# Revit family: Peak 380 Armarmatur
name_source: partatom
category: Lighting Fixtures
revit_build: Autodesk Revit 2015 (Build: 20140903_1530(x64)
units: mm (PartAtom-declared; Revit-internal decimal feet)

## types (72) — shared parameters
BIMobject category = Outside
Classification = IP 66, class II
Color Filter = 16777215
Colour accuracy = 4 steps SDCM
Colour rendering = min 70 Ra, typically 75 Ra
Connection = In the pole.The luminaire is delivered with lead according to pole height, 2x1.5 mm2
Corrosion class = C5
Design country = Denmark
Dimming = 8-100% in time intervals or 1-10 V, DALI, Line switch, AmpDim
Dimming Lamp Color Temperature Shift = <None>
Edition number = 1
Emit Shape Visible in Rendering = No
Emit from Circle Diameter = 300 mm
Height = 114 mm  [stored 0.374016 ft]
IFC Classification = Light Fixture
Impact resistance = IK08
Installation instructions = http://www.focus-lighting.dk
Length = 490 mm  [stored 1.60761 ft]
Manufacturer = Focus Lighting
Manufacturer country = Denmark
Manufacturer name = Focus Lighting
Material Secondary = Glass-Nyx
Mounting = On conical pole, 60 or 76 mm top diameter,
Nominal height = 114
Nominal width = 380
Operational life = min. 80,000 hours at ta max 25°, L80B10
Operationel life = min 100,000 hours
Product Data Url = https://bimobject.com
Product Guid = e5eea86c-a8f0-42d5-a2a8-c1225b159391
Product SKU = peak380
Product family = Outdoor
Product group = Columns
QR code = http://bimobject.com
Shade = 3 mm hardened glass, coated on the edge
Surge protection = L/N-GND: 8 kV, L-N: 6 kV
Technical description = http://www.focus-lighting.dk
Temperature range = -30 to +35° C
Tilt Angle = 90.00°
UNSPSC Code = 3911
URL = http://bimobject.com
Voltage = 220
Wattage Comments = max 85 W
Weight = 6-7 kg
Weight Net (Kg) = 7
Width = 380 mm  [stored 1.24672 ft]
zero-valued in all types: Cost

## per-type parameters (varying)
| type | Driver | Inrush current | LED with lenses | Lamp | Material Main | Output ratio | Photometric Web File |
| 8890-4740U | Xitanium Full Xi FP 40 W 0.2-0.7 A, programmable | max 22 A (50% after 290 µs) | FastFlex (FF) type III, 1, 2, or 3 modules | 1xFF type III | FocusLighting_GraphiteGrey | 91% | Peak_2xFFg3_III-X_730_LDT.ies |
| 8890-4730U | Xitanium Full Xi FP 40 W 0.2-0.7 A, programmable | max 22 A (50% after 290 µs) | FastFlex (FF) type III, 1, 2, or 3 modules | 1xFF type III | FocusLighting_GraphiteGrey | 91% | Peak_2xFFg3_III-X_730_LDT.ies |
| 8889-3730U | Xitanium Full Xi FP 150 W 0.2-0.7 A, programmable | max 53 A (50% after 300 µs) | FastFlex (FF) type PX, 1, 2, or 3 modules | 3xFF type PX | FocusLighting_Black | 90-94% | Peak_2xFFg3DA_PX_730_LDT.ies |
| 8889-3740U | Xitanium Full Xi FP 150 W 0.2-0.7 A, programmable | max 53 A (50% after 300 µs) | FastFlex (FF) type PX, 1, 2, or 3 modules | 3xFF type PX | FocusLighting_Black | 90-94% | Peak_2xFFg3DA_PX_730_LDT.ies |
| 8889-4730U | Xitanium Full Xi FP 150 W 0.2-0.7 A, programmable | max 53 A (50% after 300 µs) | FastFlex (FF) type PX, 1, 2, or 3 modules | 3xFF type PX | FocusLighting_GraphiteGrey | 90-94% | Peak_2xFFg3DA_PX_730_LDT.ies |
| 8889-4740U | Xitanium Full Xi FP 150 W 0.2-0.7 A, programmable | max 53 A (50% after 300 µs) | FastFlex (FF) type PX, 1, 2, or 3 modules | 3xFF type PX | FocusLighting_GraphiteGrey | 90-94% | Peak_2xFFg3DA_PX_730_LDT.ies |
| 8889-9730U | Xitanium Full Xi FP 150 W 0.2-0.7 A, programmable | max 53 A (50% after 300 µs) | FastFlex (FF) type PX, 1, 2, or 3 modules | 3xFF type PX | FocusLighting_SilverGrey | 90-94% | Peak_2xFFg3DA_PX_730_LDT.ies |
| 8889-9740U | Xitanium Full Xi FP 150 W 0.2-0.7 A, programmable | max 53 A (50% after 300 µs) | FastFlex (FF) type PX, 1, 2, or 3 modules | 3xFF type PX | FocusLighting_SilverGrey | 90-94% | Peak_2xFFg3DA_PX_730_LDT.ies |
| 8888-3730U | Xitanium Full Xi FP 75 W 0.2-0.7 A, programmable | max 46 A (50% after 250 µs) | FastFlex (FF) type PX, 1, 2, or 3 modules | 2xFF type PX | FocusLighting_Black | 90-94% | Peak_2xFFg3DA_PX_730_LDT.ies |
| 8888-3740U | Xitanium Full Xi FP 75 W 0.2-0.7 A, programmable | max 46 A (50% after 250 µs) | FastFlex (FF) type PX, 1, 2, or 3 modules | 2xFF type PX | FocusLighting_Black | 90-94% | Peak_2xFFg3DA_PX_730_LDT.ies |
| 8888-4730U | Xitanium Full Xi FP 75 W 0.2-0.7 A, programmable | max 46 A (50% after 250 µs) | FastFlex (FF) type PX, 1, 2, or 3 modules | 2xFF type PX | FocusLighting_GraphiteGrey | 90-94% | Peak_2xFFg3DA_PX_730_LDT.ies |
| 8888-4740U | Xitanium Full Xi FP 75 W 0.2-0.7 A, programmable | max 46 A (50% after 250 µs) | FastFlex (FF) type PX, 1, 2, or 3 modules | 2xFF type PX | FocusLighting_GraphiteGrey | 90-94% | Peak_2xFFg3DA_PX_730_LDT.ies |
| 8888-9730U | Xitanium Full Xi FP 75 W 0.2-0.7 A, programmable | max 46 A (50% after 250 µs) | FastFlex (FF) type PX, 1, 2, or 3 modules | 2xFF type PX | FocusLighting_SilverGrey | 90-94% | Peak_2xFFg3DA_PX_730_LDT.ies |
| 8888-9740U | Xitanium Full Xi FP 75 W 0.2-0.7 A, programmable | max 46 A (50% after 250 µs) | FastFlex (FF) type PX, 1, 2, or 3 modules | 2xFF type PX | FocusLighting_SilverGrey | 90-94% | Peak_2xFFg3DA_PX_730_LDT.ies |
| 8887-3730U | Xitanium Full Xi FP 40 W 0.2-0.7 A, programmable | max 22 A (50% after 290 µs) | FastFlex (FF) type PX, 1, 2, or 3 modules | 1xFF type PX | FocusLighting_Black | 90-94% | Peak_2xFFg3DA_PX_730_LDT.ies |
| 8887-3740U | Xitanium Full Xi FP 40 W 0.2-0.7 A, programmable | max 22 A (50% after 290 µs) | FastFlex (FF) type PX, 1, 2, or 3 modules | 1xFF type PX | FocusLighting_Black | 90-94% | Peak_2xFFg3DA_PX_730_LDT.ies |
| 8887-4730U | Xitanium Full Xi FP 40 W 0.2-0.7 A, programmable | max 22 A (50% after 290 µs) | FastFlex (FF) type PX, 1, 2, or 3 modules | 1xFF type PX | FocusLighting_GraphiteGrey | 90-94% | Peak_2xFFg3DA_PX_730_LDT.ies |
| 8887-4740U | Xitanium Full Xi FP 40 W 0.2-0.7 A, programmable | max 22 A (50% after 290 µs) | FastFlex (FF) type PX, 1, 2, or 3 modules | 1xFF type PX | FocusLighting_GraphiteGrey | 90-94% | Peak_2xFFg3DA_PX_730_LDT.ies |
| 8887-9730U | Xitanium Full Xi FP 40 W 0.2-0.7 A, programmable | max 22 A (50% after 290 µs) | FastFlex (FF) type PX, 1, 2, or 3 modules | 1xFF type PX | FocusLighting_SilverGrey | 90-94% | Peak_2xFFg3DA_PX_730_LDT.ies |
| 8887-9740U | Xitanium Full Xi FP 40 W 0.2-0.7 A, programmable | max 22 A (50% after 290 µs) | FastFlex (FF) type PX, 1, 2, or 3 modules | 1xFF type PX | FocusLighting_SilverGrey | 90-94% | Peak_2xFFg3DA_PX_730_LDT.ies |
| 8898-3730U | Xitanium Full Xi FP 150 W 0.2-0.7 A, programmable | max 53 A (50% after 300 µs) | FastFlex (FF) type IV, 1, 2, or 3 modules | 3xFF type IV | FocusLighting_Black | 90-94% | Peak_2xFFg3_IV-X_730_LDT.ies |
| 8898-3740U | Xitanium Full Xi FP 150 W 0.2-0.7 A, programmable | max 53 A (50% after 300 µs) | FastFlex (FF) type IV, 1, 2, or 3 modules | 3xFF type IV | FocusLighting_Black | 90-94% | Peak_2xFFg3_IV-X_730_LDT.ies |
| 8898-4730U | Xitanium Full Xi FP 150 W 0.2-0.7 A, programmable | max 53 A (50% after 300 µs) | FastFlex (FF) type IV, 1, 2, or 3 modules | 3xFF type IV | FocusLighting_GraphiteGrey | 90-94% | Peak_2xFFg3_IV-X_730_LDT.ies |
| 8898-4740U | Xitanium Full Xi FP 150 W 0.2-0.7 A, programmable | max 53 A (50% after 300 µs) | FastFlex (FF) type IV, 1, 2, or 3 modules | 3xFF type IV | FocusLighting_GraphiteGrey | 90-94% | Peak_2xFFg3_IV-X_730_LDT.ies |
| 8898-9730U | Xitanium Full Xi FP 150 W 0.2-0.7 A, programmable | max 53 A (50% after 300 µs) | FastFlex (FF) type IV, 1, 2, or 3 modules | 3xFF type IV | FocusLighting_SilverGrey | 90-94% | Peak_2xFFg3_IV-X_730_LDT.ies |
| 8898-9740U | Xitanium Full Xi FP 150 W 0.2-0.7 A, programmable | max 53 A (50% after 300 µs) | FastFlex (FF) type IV, 1, 2, or 3 modules | 3xFF type IV | FocusLighting_SilverGrey | 90-94% | Peak_2xFFg3_IV-X_730_LDT.ies |
| 8897-3730U | Xitanium Full Xi FP 75 W 0.2-0.7 A, programmable | max 46 A (50% after 250 µs) | FastFlex (FF) type IV, 1, 2, or 3 modules | 2xFF type IV | FocusLighting_Black | 90-94% | Peak_2xFFg3_IV-X_730_LDT.ies |
| 8897-3740U | Xitanium Full Xi FP 75 W 0.2-0.7 A, programmable | max 46 A (50% after 250 µs) | FastFlex (FF) type IV, 1, 2, or 3 modules | 2xFF type IV | FocusLighting_Black | 90-94% | Peak_2xFFg3_IV-X_730_LDT.ies |
| 8897-4730U | Xitanium Full Xi FP 75 W 0.2-0.7 A, programmable | max 46 A (50% after 250 µs) | FastFlex (FF) type IV, 1, 2, or 3 modules | 2xFF type IV | FocusLighting_GraphiteGrey | 90-94% | Peak_2xFFg3_IV-X_730_LDT.ies |
| 8897-4740U | Xitanium Full Xi FP 75 W 0.2-0.7 A, programmable | max 46 A (50% after 250 µs) | FastFlex (FF) type IV, 1, 2, or 3 modules | 2xFF type IV | FocusLighting_GraphiteGrey | 90-94% | Peak_2xFFg3_IV-X_730_LDT.ies |
| 8897-9730U | Xitanium Full Xi FP 75 W 0.2-0.7 A, programmable | max 46 A (50% after 250 µs) | FastFlex (FF) type IV, 1, 2, or 3 modules | 2xFF type IV | FocusLighting_SilverGrey | 90-94% | Peak_2xFFg3_IV-X_730_LDT.ies |
| 8897-9740U | Xitanium Full Xi FP 75 W 0.2-0.7 A, programmable | max 46 A (50% after 250 µs) | FastFlex (FF) type IV, 1, 2, or 3 modules | 2xFF type IV | FocusLighting_SilverGrey | 90-94% | Peak_2xFFg3_IV-X_730_LDT.ies |
| 8896-3730U | Xitanium Full Xi FP 40 W 0.2-0.7 A, programmable | max 22 A (50% after 290 µs) | FastFlex (FF) type IV, 1, 2, or 3 modules | 1xFF type IV | FocusLighting_Black | 90-94% | Peak_2xFFg3_IV-X_730_LDT.ies |
| 8896-3740U | Xitanium Full Xi FP 40 W 0.2-0.7 A, programmable | max 22 A (50% after 290 µs) | FastFlex (FF) type IV, 1, 2, or 3 modules | 1xFF type IV | FocusLighting_Black | 90-94% | Peak_2xFFg3_IV-X_730_LDT.ies |
| 8896-4730U | Xitanium Full Xi FP 40 W 0.2-0.7 A, programmable | max 22 A (50% after 290 µs) | FastFlex (FF) type IV, 1, 2, or 3 modules | 1xFF type IV | FocusLighting_GraphiteGrey | 90-94% | Peak_2xFFg3_IV-X_730_LDT.ies |
| 8896-4740U | Xitanium Full Xi FP 40 W 0.2-0.7 A, programmable | max 22 A (50% after 290 µs) | FastFlex (FF) type IV, 1, 2, or 3 modules | 1xFF type IV | FocusLighting_GraphiteGrey | 90-94% | Peak_2xFFg3_IV-X_730_LDT.ies |
| 8896-9730U | Xitanium Full Xi FP 40 W 0.2-0.7 A, programmable | max 22 A (50% after 290 µs) | FastFlex (FF) type IV, 1, 2, or 3 modules | 1xFF type IV | FocusLighting_SilverGrey | 90-94% | Peak_2xFFg3_IV-X_730_LDT.ies |
| 8896-9740U | Xitanium Full Xi FP 40 W 0.2-0.7 A, programmable | max 22 A (50% after 290 µs) | FastFlex (FF) type IV, 1, 2, or 3 modules | 1xFF type IV | FocusLighting_SilverGrey | 90-94% | Peak_2xFFg3_IV-X_730_LDT.ies |
| 8895-3730U | Xitanium Full Xi FP 150 W 0.2-0.7 A, programmable | max 53 A (50% after 300 µs) | FastFlex (FF) type II-XWTR, 1, 2, or 3 modules | 3xFF type II-XWTR | FocusLighting_Black | 94% | Peak_2xFFg3_II-X WTR_730_LDT.ies |
| 8895-3740U | Xitanium Full Xi FP 150 W 0.2-0.7 A, programmable | max 53 A (50% after 300 µs) | FastFlex (FF) type II-XWTR, 1, 2, or 3 modules | 3xFF type II-XWTR | FocusLighting_Black | 94% | Peak_2xFFg3_II-X WTR_730_LDT.ies |
| 8895-4730U | Xitanium Full Xi FP 150 W 0.2-0.7 A, programmable | max 53 A (50% after 300 µs) | FastFlex (FF) type II-XWTR, 1, 2, or 3 modules | 3xFF type II-XWTR | FocusLighting_GraphiteGrey | 94% | Peak_2xFFg3_II-X WTR_730_LDT.ies |
| 8895-4740U | Xitanium Full Xi FP 150 W 0.2-0.7 A, programmable | max 53 A (50% after 300 µs) | FastFlex (FF) type II-XWTR, 1, 2, or 3 modules | 3xFF type II-XWTR | FocusLighting_GraphiteGrey | 94% | Peak_2xFFg3_II-X WTR_730_LDT.ies |
| 8895-9730U | Xitanium Full Xi FP 150 W 0.2-0.7 A, programmable | max 53 A (50% after 300 µs) | FastFlex (FF) type II-XWTR, 1, 2, or 3 modules | 3xFF type II-XWTR | FocusLighting_SilverGrey | 94% | Peak_2xFFg3_II-X WTR_730_LDT.ies |
| 8895-9740U | Xitanium Full Xi FP 150 W 0.2-0.7 A, programmable | max 53 A (50% after 300 µs) | FastFlex (FF) type II-XWTR, 1, 2, or 3 modules | 3xFF type II-XWTR | FocusLighting_SilverGrey | 94% | Peak_2xFFg3_II-X WTR_730_LDT.ies |
| 8894-3730U | Xitanium Full Xi FP 75 W 0.2-0.7 A, programmable | max 46 A (50% after 250 µs) | FastFlex (FF) type II-XWTR, 1, 2, or 3 modules | 2xFF type II-XWTR | FocusLighting_Black | 94% | Peak_2xFFg3_II-X WTR_730_LDT.ies |
| 8894-3740U | Xitanium Full Xi FP 75 W 0.2-0.7 A, programmable | max 46 A (50% after 250 µs) | FastFlex (FF) type II-XWTR, 1, 2, or 3 modules | 2xFF type II-XWTR | FocusLighting_Black | 94% | Peak_2xFFg3_II-X WTR_730_LDT.ies |
| 8894-4730U | Xitanium Full Xi FP 75 W 0.2-0.7 A, programmable | max 46 A (50% after 250 µs) | FastFlex (FF) type II-XWTR, 1, 2, or 3 modules | 2xFF type II-XWTR | FocusLighting_GraphiteGrey | 94% | Peak_2xFFg3_II-X WTR_730_LDT.ies |
| 8894-4740U | Xitanium Full Xi FP 75 W 0.2-0.7 A, programmable | max 46 A (50% after 250 µs) | FastFlex (FF) type II-XWTR, 1, 2, or 3 modules | 2xFF type II-XWTR | FocusLighting_GraphiteGrey | 94% | Peak_2xFFg3_II-X WTR_730_LDT.ies |
| 8894-9730U | Xitanium Full Xi FP 75 W 0.2-0.7 A, programmable | max 46 A (50% after 250 µs) | FastFlex (FF) type II-XWTR, 1, 2, or 3 modules | 2xFF type II-XWTR | FocusLighting_SilverGrey | 94% | Peak_2xFFg3_II-X WTR_730_LDT.ies |
| 8894-9740U | Xitanium Full Xi FP 75 W 0.2-0.7 A, programmable | max 46 A (50% after 250 µs) | FastFlex (FF) type II-XWTR, 1, 2, or 3 modules | 2xFF type II-XWTR | FocusLighting_SilverGrey | 94% | Peak_2xFFg3_II-X WTR_730_LDT.ies |
| 8893-3730U | Xitanium Full Xi FP 40 W 0.2-0.7 A, programmable | max 22 A (50% after 290 µs) | FastFlex (FF) type II-XWTR, 1, 2, or 3 modules | 1xFF type II-XWTR | FocusLighting_Black | 94% | Peak_2xFFg3_II-X WTR_730_LDT.ies |
| 8893-3740U | Xitanium Full Xi FP 40 W 0.2-0.7 A, programmable | max 22 A (50% after 290 µs) | FastFlex (FF) type II-XWTR, 1, 2, or 3 modules | 1xFF type II-XWTR | FocusLighting_Black | 94% | Peak_2xFFg3_II-X WTR_730_LDT.ies |
| 8893-4730U | Xitanium Full Xi FP 40 W 0.2-0.7 A, programmable | max 22 A (50% after 290 µs) | FastFlex (FF) type II-XWTR, 1, 2, or 3 modules | 1xFF type II-XWTR | FocusLighting_GraphiteGrey | 94% | Peak_2xFFg3_II-X WTR_730_LDT.ies |
| 8893-4740U | Xitanium Full Xi FP 40 W 0.2-0.7 A, programmable | max 22 A (50% after 290 µs) | FastFlex (FF) type II-XWTR, 1, 2, or 3 modules | 1xFF type II-XWTR | FocusLighting_GraphiteGrey | 94% | Peak_2xFFg3_II-X WTR_730_LDT.ies |
| 8893-9730U | Xitanium Full Xi FP 40 W 0.2-0.7 A, programmable | max 22 A (50% after 290 µs) | FastFlex (FF) type II-XWTR, 1, 2, or 3 modules | 1xFF type II-XWTR | FocusLighting_SilverGrey | 94% | Peak_2xFFg3_II-X WTR_730_LDT.ies |
| 8893-9740U | Xitanium Full Xi FP 40 W 0.2-0.7 A, programmable | max 22 A (50% after 290 µs) | FastFlex (FF) type II-XWTR, 1, 2, or 3 modules | 1xFF type II-XWTR | FocusLighting_SilverGrey | 94% | Peak_2xFFg3_II-X WTR_730_LDT.ies |
| 8892-3730U | Xitanium Full Xi FP 150 W 0.2-0.7 A, programmable | max 53 A (50% after 300 µs) | FastFlex (FF) type III, 1, 2, or 3 modules | 3xFF type III | FocusLighting_Black | 91% | Peak_2xFFg3_III-X_730_LDT.ies |
| 8892-3740U | Xitanium Full Xi FP 150 W 0.2-0.7 A, programmable | max 53 A (50% after 300 µs) | FastFlex (FF) type III, 1, 2, or 3 modules | 3xFF type III | FocusLighting_Black | 91% | Peak_2xFFg3_III-X_730_LDT.ies |
| 8892-4730U | Xitanium Full Xi FP 150 W 0.2-0.7 A, programmable | max 53 A (50% after 300 µs) | FastFlex (FF) type III, 1, 2, or 3 modules | 3xFF type III | FocusLighting_GraphiteGrey | 91% | Peak_2xFFg3_III-X_730_LDT.ies |
| 8892-4740U | Xitanium Full Xi FP 150 W 0.2-0.7 A, programmable | max 53 A (50% after 300 µs) | FastFlex (FF) type III, 1, 2, or 3 modules | 3xFF type III | FocusLighting_GraphiteGrey | 91% | Peak_2xFFg3_III-X_730_LDT.ies |
| 8892-9730U | Xitanium Full Xi FP 150 W 0.2-0.7 A, programmable | max 53 A (50% after 300 µs) | FastFlex (FF) type III, 1, 2, or 3 modules | 3xFF type III | FocusLighting_SilverGrey | 91% | Peak_2xFFg3_III-X_730_LDT.ies |
| 8892-9740U | Xitanium Full Xi FP 150 W 0.2-0.7 A, programmable | max 53 A (50% after 300 µs) | FastFlex (FF) type III, 1, 2, or 3 modules | 3xFF type III | FocusLighting_SilverGrey | 91% | Peak_2xFFg3_III-X_730_LDT.ies |
| 8891-3730U | Xitanium Full Xi FP 75 W 0.2-0.7 A, programmable | max 46 A (50% after 250 µs) | FastFlex (FF) type III, 1, 2, or 3 modules | 2xFF type III | FocusLighting_Black | 91% | Peak_2xFFg3_III-X_730_LDT.ies |
| 8891-3740U | Xitanium Full Xi FP 75 W 0.2-0.7 A, programmable | max 46 A (50% after 250 µs) | FastFlex (FF) type III, 1, 2, or 3 modules | 2xFF type III | FocusLighting_Black | 91% | Peak_2xFFg3_III-X_730_LDT.ies |
| 8891-4730U | Xitanium Full Xi FP 75 W 0.2-0.7 A, programmable | max 46 A (50% after 250 µs) | FastFlex (FF) type III, 1, 2, or 3 modules | 2xFF type III | FocusLighting_GraphiteGrey | 91% | Peak_2xFFg3_III-X_730_LDT.ies |
| 8891-4740U | Xitanium Full Xi FP 75 W 0.2-0.7 A, programmable | max 46 A (50% after 250 µs) | FastFlex (FF) type III, 1, 2, or 3 modules | 2xFF type III | FocusLighting_GraphiteGrey | 91% | Peak_2xFFg3_III-X_730_LDT.ies |
| 8891-9730U | Xitanium Full Xi FP 75 W 0.2-0.7 A, programmable | max 46 A (50% after 250 µs) | FastFlex (FF) type III, 1, 2, or 3 modules | 2xFF type III | FocusLighting_SilverGrey | 91% | Peak_2xFFg3_III-X_730_LDT.ies |
| 8891-9740U | Xitanium Full Xi FP 75 W 0.2-0.7 A, programmable | max 46 A (50% after 250 µs) | FastFlex (FF) type III, 1, 2, or 3 modules | 2xFF type III | FocusLighting_SilverGrey | 91% | Peak_2xFFg3_III-X_730_LDT.ies |
| 8890-3730U | Xitanium Full Xi FP 40 W 0.2-0.7 A, programmable | max 22 A (50% after 290 µs) | FastFlex (FF) type III, 1, 2, or 3 modules | 1xFF type III | FocusLighting_Black | 91% | Peak_2xFFg3_III-X_730_LDT.ies |
| 8890-3740U | Xitanium Full Xi FP 40 W 0.2-0.7 A, programmable | max 22 A (50% after 290 µs) | FastFlex (FF) type III, 1, 2, or 3 modules | 1xFF type III | FocusLighting_Black | 91% | Peak_2xFFg3_III-X_730_LDT.ies |
| 8890-9730U | Xitanium Full Xi FP 40 W 0.2-0.7 A, programmable | max 22 A (50% after 290 µs) | FastFlex (FF) type III, 1, 2, or 3 modules | 1xFF type III | FocusLighting_SilverGrey | 91% | Peak_2xFFg3_III-X_730_LDT.ies |
| 8890-9740U | Xitanium Full Xi FP 40 W 0.2-0.7 A, programmable | max 22 A (50% after 290 µs) | FastFlex (FF) type III, 1, 2, or 3 modules | 1xFF type III | FocusLighting_SilverGrey | 91% | Peak_2xFFg3_III-X_730_LDT.ies |

note: [stored X ft] marks values corroborated as IEEE doubles in the binary element streams (Revit-internal decimal feet)

## geometry (parser evidence)
native form markers: Blend x8, Sweep x4
no freeform markers — native parametric forms only
